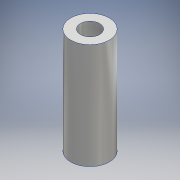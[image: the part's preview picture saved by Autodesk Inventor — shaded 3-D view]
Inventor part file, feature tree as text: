
AUTODESK INVENTOR PART (.ipt)
format: ipt  version: 2016 (Build 200138000, 138)  size: 108,544 bytes
history: native  units: mm
features: sketch x2, extrude x2, hole x2, other x1
ambient origin geometry x8: Origin, YZ Plane, XZ Plane, XY Plane, X Axis, Y Axis, Z Axis, Center Point
bodies: Body1 (feature_tree)
feature tree (7):
  other  "ソリッド1"
  sketch  "スケッチ1"
  extrude  "押し出し1"  Depth=8.0mm
  sketch  "スケッチ2"
  extrude  "押し出し2"  Depth=4.001mm
  hole  "穴1"  [1 undecoded]
  hole  "穴2"  [1 undecoded]
note: 2 required parameter values undecoded (feature->parameter linkage not recoverable at this tier; creation-order binding heuristic only, values carry confidence <= 0.55)
